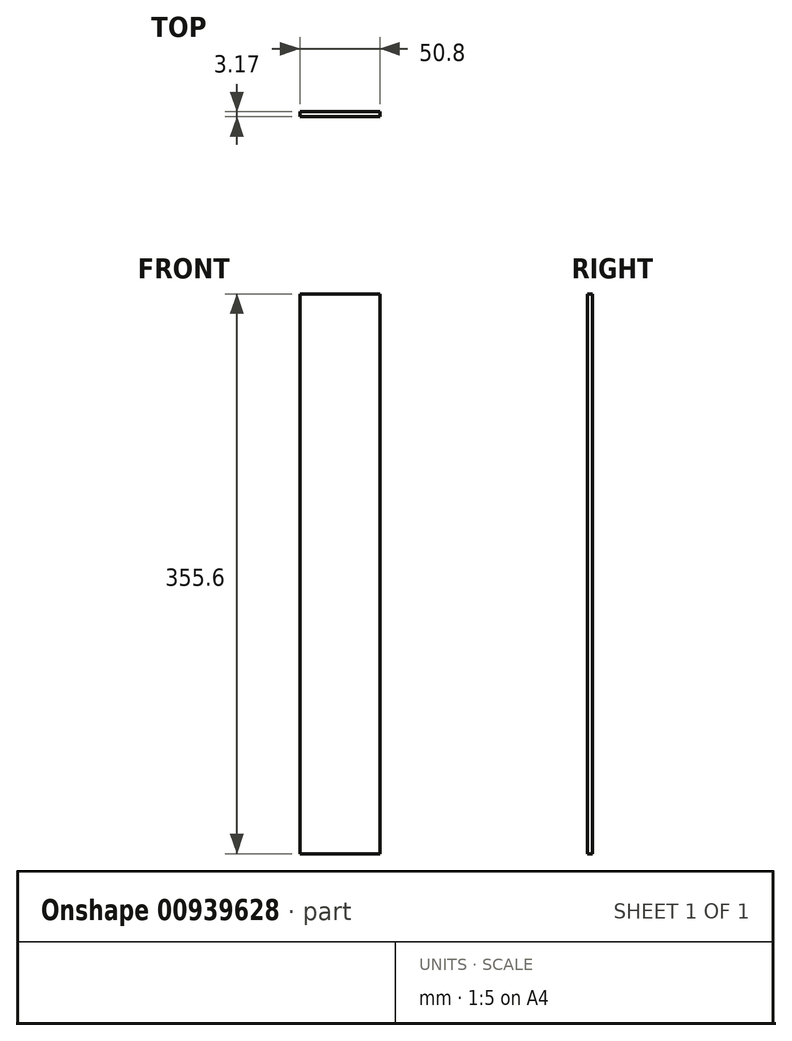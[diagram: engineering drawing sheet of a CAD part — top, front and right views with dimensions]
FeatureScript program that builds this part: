
annotation { "Feature Type Name" : "Feature", "Feature Type Description" : "" }
export const myFeature = defineFeature(function(context is Context, id is Id, definition is map)
    precondition{}
    {
        {
            var Q0;
            Q0=qCreatedBy(makeId("Front.planeOp"),FACE);
            var sketch = newSketch(context, id + "F0", { "sketchPlane" : qUnion([Q0])});
            skLineSegment(sketch, "E0.bottom", {"start": v(0, 0) * mm, "end": v(-50.8, 0) * mm});
            skLineSegment(sketch, "E0.top", {"start": v(0, 355.6) * mm, "end": v(-50.8, 355.6) * mm});
            skLineSegment(sketch, "E0.left", {"start": v(0, 0) * mm, "end": v(0, 355.6) * mm});
            skLineSegment(sketch, "E0.right", {"start": v(-50.8, 0) * mm, "end": v(-50.8, 355.6) * mm});
            skSolve(sketch);
        }
        {
            var Q0;
            Q0 = qSketchRegion(id + "F0", true);
            extrude(context, id + "F1", {"entities" : qUnion([Q0]), "oppositeDirection" : true, "depth" : 3.17 * mm, "offsetDistance" : 25.4 * mm});
        }
    });
